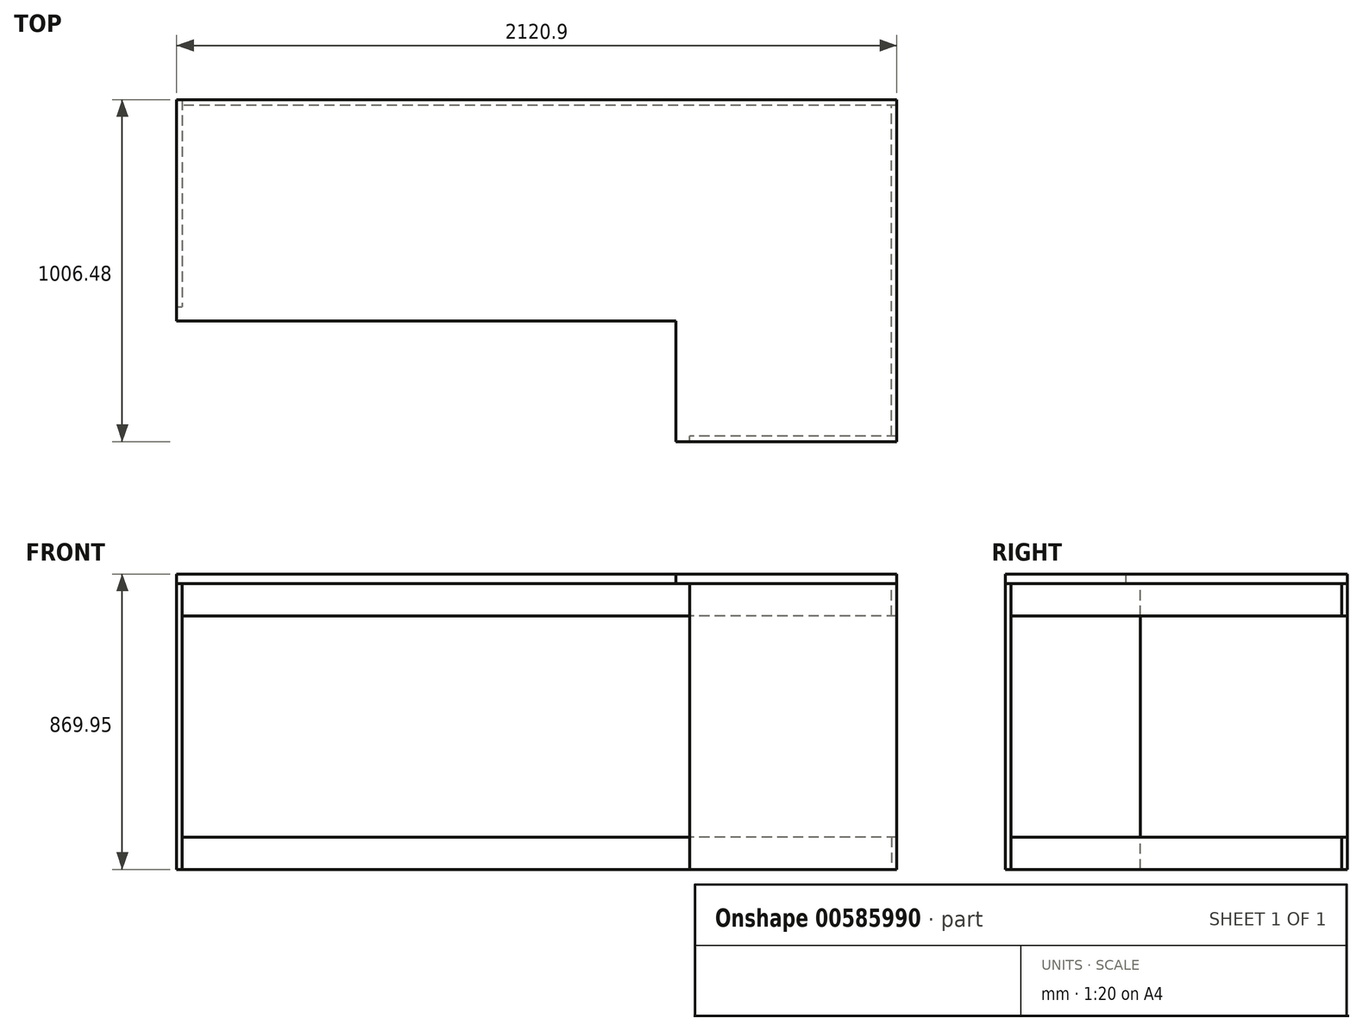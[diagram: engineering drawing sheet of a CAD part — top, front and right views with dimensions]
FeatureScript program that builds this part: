
annotation { "Feature Type Name" : "Feature", "Feature Type Description" : "" }
export const myFeature = defineFeature(function(context is Context, id is Id, definition is map)
    precondition{}
    {
        {
            var Q0;
            Q0=qCreatedBy(makeId("Top.planeOp"),FACE);
            cPlane(context, id + "F0", {"entities" : qUnion([Q0]), "cplaneType" : CPlaneType.OFFSET, "offset" : 914.4 * mm, "width" : 152.4 * mm, "height" : 152.4 * mm});
        }
        {
            var Q0;
            Q0=qCreatedBy(id+"F0.planeOp",FACE);
            var sketch = newSketch(context, id + "F1", { "sketchPlane" : qUnion([Q0])});
            skLineSegment(sketch, "E0.bottom", {"start": v(-1060.45, 325.44) * mm, "end": v(1060.45, 325.44) * mm});
            skLineSegment(sketch, "E0.top", {"start": v(-1060.45, -325.44) * mm, "end": v(1060.45, -325.44) * mm});
            skLineSegment(sketch, "E0.left", {"start": v(-1060.45, 325.44) * mm, "end": v(-1060.45, -325.44) * mm});
            skLineSegment(sketch, "E0.right", {"start": v(1060.45, 325.44) * mm, "end": v(1060.45, -325.44) * mm});
            skPoint(sketch, "E0.middle", {"position": v(0, 0) * mm});
            skSolve(sketch);
        }
        {
            var Q0;
            Q0 = qSketchRegion(id + "F1", true);
            extrude(context, id + "F2", {"entities" : qUnion([Q0]), "oppositeDirection" : true, "depth" : 28.57 * mm, "offsetDistance" : 25.4 * mm});
        }
        {
            var Q0;
            Q0=makeQuery(id+"F2.opExtrude","SWEPT_FACE",FACE,{"disambiguationData":[OSD([sQuery(id+"F1.wireOp",EDGE,"E0.top")])]});
            var sketch = newSketch(context, id + "F3", { "sketchPlane" : qUnion([Q0])});
            skLineSegment(sketch, "E1.bottom", {"start": v(1060.45, 914.4) * mm, "end": v(409.58, 914.4) * mm});
            skLineSegment(sketch, "E1.top", {"start": v(1060.45, 885.83) * mm, "end": v(409.58, 885.83) * mm});
            skLineSegment(sketch, "E1.left", {"start": v(1060.45, 914.4) * mm, "end": v(1060.45, 885.83) * mm});
            skLineSegment(sketch, "E1.right", {"start": v(409.58, 914.4) * mm, "end": v(409.58, 885.83) * mm});
            skSolve(sketch);
        }
        {
            var Q0;
            Q0 = qSketchRegion(id + "F3", true);
            extrude(context, id + "F4", {"entities" : qUnion([Q0]), "operationType" : NewBodyOperationType.ADD, "depth" : 355.6 * mm, "offsetDistance" : 25.4 * mm});
        }
        {
            var Q0;
            Q0=makeQuery(id+"F4.boolean.opBoolean","MERGE",FACE,{"derivedFrom":[makeQuery(id+"F2.opExtrude","CAP_FACE",FACE,{"disambiguationData":[OSD([sQuery(id+"F1.wireOp",EDGE,"E0.bottom"),sQuery(id+"F1.wireOp",EDGE,"E0.top"),sQuery(id+"F1.wireOp",EDGE,"E0.left"),sQuery(id+"F1.wireOp",EDGE,"E0.right")])],"isStart":false}),makeQuery(id+"F4.opExtrude","SWEPT_FACE",FACE,{"disambiguationData":[OSD([sQuery(id+"F3.wireOp",EDGE,"E1.top")])]})]});
            var sketch = newSketch(context, id + "F5", { "sketchPlane" : qUnion([Q0])});
            skLineSegment(sketch, "E2.bottom", {"start": v(-1060.45, -325.44) * mm, "end": v(-1044.58, -325.44) * mm});
            skLineSegment(sketch, "E2.top", {"start": v(-1060.45, 284.16) * mm, "end": v(-1044.58, 284.16) * mm});
            skLineSegment(sketch, "E2.left", {"start": v(-1060.45, -325.44) * mm, "end": v(-1060.45, 284.16) * mm});
            skLineSegment(sketch, "E2.right", {"start": v(-1044.58, -325.44) * mm, "end": v(-1044.58, 284.16) * mm});
            skSolve(sketch);
        }
        {
            var Q0;
            Q0 = qSketchRegion(id + "F5", true);
            extrude(context, id + "F6", {"entities" : qUnion([Q0]), "depth" : 841.38 * mm, "offsetDistance" : 25.4 * mm});
        }
        {
            var Q0;
            Q0=makeQuery(id+"F4.boolean.opBoolean","MERGE",FACE,{"derivedFrom":[makeQuery(id+"F2.opExtrude","CAP_FACE",FACE,{"disambiguationData":[OSD([sQuery(id+"F1.wireOp",EDGE,"E0.bottom"),sQuery(id+"F1.wireOp",EDGE,"E0.top"),sQuery(id+"F1.wireOp",EDGE,"E0.left"),sQuery(id+"F1.wireOp",EDGE,"E0.right")])],"isStart":false}),makeQuery(id+"F4.opExtrude","SWEPT_FACE",FACE,{"disambiguationData":[OSD([sQuery(id+"F3.wireOp",EDGE,"E1.top")])]})]});
            var sketch = newSketch(context, id + "F7", { "sketchPlane" : qUnion([Q0])});
            skLineSegment(sketch, "E3.bottom", {"start": v(1060.45, 681.04) * mm, "end": v(450.85, 681.04) * mm});
            skLineSegment(sketch, "E3.top", {"start": v(1060.45, 665.16) * mm, "end": v(450.85, 665.16) * mm});
            skLineSegment(sketch, "E3.left", {"start": v(1060.45, 681.04) * mm, "end": v(1060.45, 665.16) * mm});
            skLineSegment(sketch, "E3.right", {"start": v(450.85, 681.04) * mm, "end": v(450.85, 665.16) * mm});
            skSolve(sketch);
        }
        {
            var Q0;
            Q0 = qSketchRegion(id + "F7", true);
            extrude(context, id + "F8", {"entities" : qUnion([Q0]), "depth" : 841.38 * mm, "offsetDistance" : 25.4 * mm});
        }
        {
            var Q0;
            Q0=makeQuery(id+"F6.opExtrude","SWEPT_FACE",FACE,{"disambiguationData":[OSD([sQuery(id+"F5.wireOp",EDGE,"E2.right")])]});
            var sketch = newSketch(context, id + "F9", { "sketchPlane" : qUnion([Q0])});
            skLineSegment(sketch, "E4.bottom", {"start": v(325.44, 885.83) * mm, "end": v(309.56, 885.83) * mm});
            skLineSegment(sketch, "E4.top", {"start": v(325.44, 790.58) * mm, "end": v(309.56, 790.58) * mm});
            skLineSegment(sketch, "E4.left", {"start": v(325.44, 885.83) * mm, "end": v(325.44, 790.58) * mm});
            skLineSegment(sketch, "E4.right", {"start": v(309.56, 885.83) * mm, "end": v(309.56, 790.58) * mm});
            skSolve(sketch);
        }
        {
            var Q0;
            Q0 = qSketchRegion(id + "F9", true);
            extrude(context, id + "F10", {"entities" : qUnion([Q0]), "depth" : 2105.03 * mm, "offsetDistance" : 25.4 * mm});
        }
        {
            var Q0;
            Q0=makeQuery(id+"F6.opExtrude","SWEPT_FACE",FACE,{"disambiguationData":[OSD([sQuery(id+"F5.wireOp",EDGE,"E2.right")])]});
            var sketch = newSketch(context, id + "F11", { "sketchPlane" : qUnion([Q0])});
            skLineSegment(sketch, "E5.bottom", {"start": v(325.44, 44.45) * mm, "end": v(309.56, 44.45) * mm});
            skLineSegment(sketch, "E5.top", {"start": v(325.44, 139.7) * mm, "end": v(309.56, 139.7) * mm});
            skLineSegment(sketch, "E5.left", {"start": v(325.44, 44.45) * mm, "end": v(325.44, 139.7) * mm});
            skLineSegment(sketch, "E5.right", {"start": v(309.56, 44.45) * mm, "end": v(309.56, 139.7) * mm});
            skSolve(sketch);
        }
        {
            var Q0;
            Q0 = qSketchRegion(id + "F11", true);
            extrude(context, id + "F12", {"entities" : qUnion([Q0]), "depth" : 2105.03 * mm, "offsetDistance" : 25.4 * mm});
        }
        {
            var Q0;
            Q0=makeQuery(id+"F12.opExtrude","SWEPT_FACE",FACE,{"disambiguationData":[OSD([sQuery(id+"F11.wireOp",EDGE,"E5.right")])]});
            var sketch = newSketch(context, id + "F13", { "sketchPlane" : qUnion([Q0])});
            skLineSegment(sketch, "E6.bottom", {"start": v(1060.45, 139.7) * mm, "end": v(1044.58, 139.7) * mm});
            skLineSegment(sketch, "E6.top", {"start": v(1060.45, 44.45) * mm, "end": v(1044.58, 44.45) * mm});
            skLineSegment(sketch, "E6.left", {"start": v(1060.45, 139.7) * mm, "end": v(1060.45, 44.45) * mm});
            skLineSegment(sketch, "E6.right", {"start": v(1044.58, 139.7) * mm, "end": v(1044.58, 44.45) * mm});
            skSolve(sketch);
        }
        {
            var Q0;
            Q0 = qSketchRegion(id + "F13", true);
            extrude(context, id + "F14", {"entities" : qUnion([Q0]), "depth" : 974.72 * mm, "offsetDistance" : 25.4 * mm});
        }
        {
            var Q0;
            Q0=makeQuery(id+"F10.opExtrude","SWEPT_FACE",FACE,{"disambiguationData":[OSD([sQuery(id+"F9.wireOp",EDGE,"E4.right")])]});
            var sketch = newSketch(context, id + "F15", { "sketchPlane" : qUnion([Q0])});
            skLineSegment(sketch, "E7.bottom", {"start": v(1060.45, 790.58) * mm, "end": v(1044.58, 790.58) * mm});
            skLineSegment(sketch, "E7.top", {"start": v(1060.45, 885.82) * mm, "end": v(1044.58, 885.82) * mm});
            skLineSegment(sketch, "E7.left", {"start": v(1060.45, 790.58) * mm, "end": v(1060.45, 885.82) * mm});
            skLineSegment(sketch, "E7.right", {"start": v(1044.58, 790.58) * mm, "end": v(1044.58, 885.82) * mm});
            skSolve(sketch);
        }
        {
            var Q0;
            Q0 = qSketchRegion(id + "F15", true);
            extrude(context, id + "F16", {"entities" : qUnion([Q0]), "depth" : 974.72 * mm, "offsetDistance" : 25.4 * mm});
        }
    });
